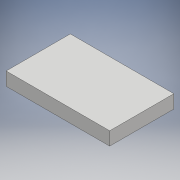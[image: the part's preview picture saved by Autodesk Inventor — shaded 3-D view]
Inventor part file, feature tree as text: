
AUTODESK INVENTOR PART (.ipt)
format: ipt  version: 2017 (Build 210142000, 142)  size: 87,552 bytes
history: native  units: mm
features: extrude x1, sketch x1
ambient origin geometry x8: Origin, YZ Plane, XZ Plane, XY Plane, X Axis, Y Axis, Z Axis, Center Point
bodies: Solid1 (feature_tree)
feature tree (2):
  extrude  "Extrusion1"  Depth=2900.0mm
  sketch  "Sketch1"  dims[d0=4680.0mm d1=2900.0mm d2=600.0mm d3=0.0mm]
